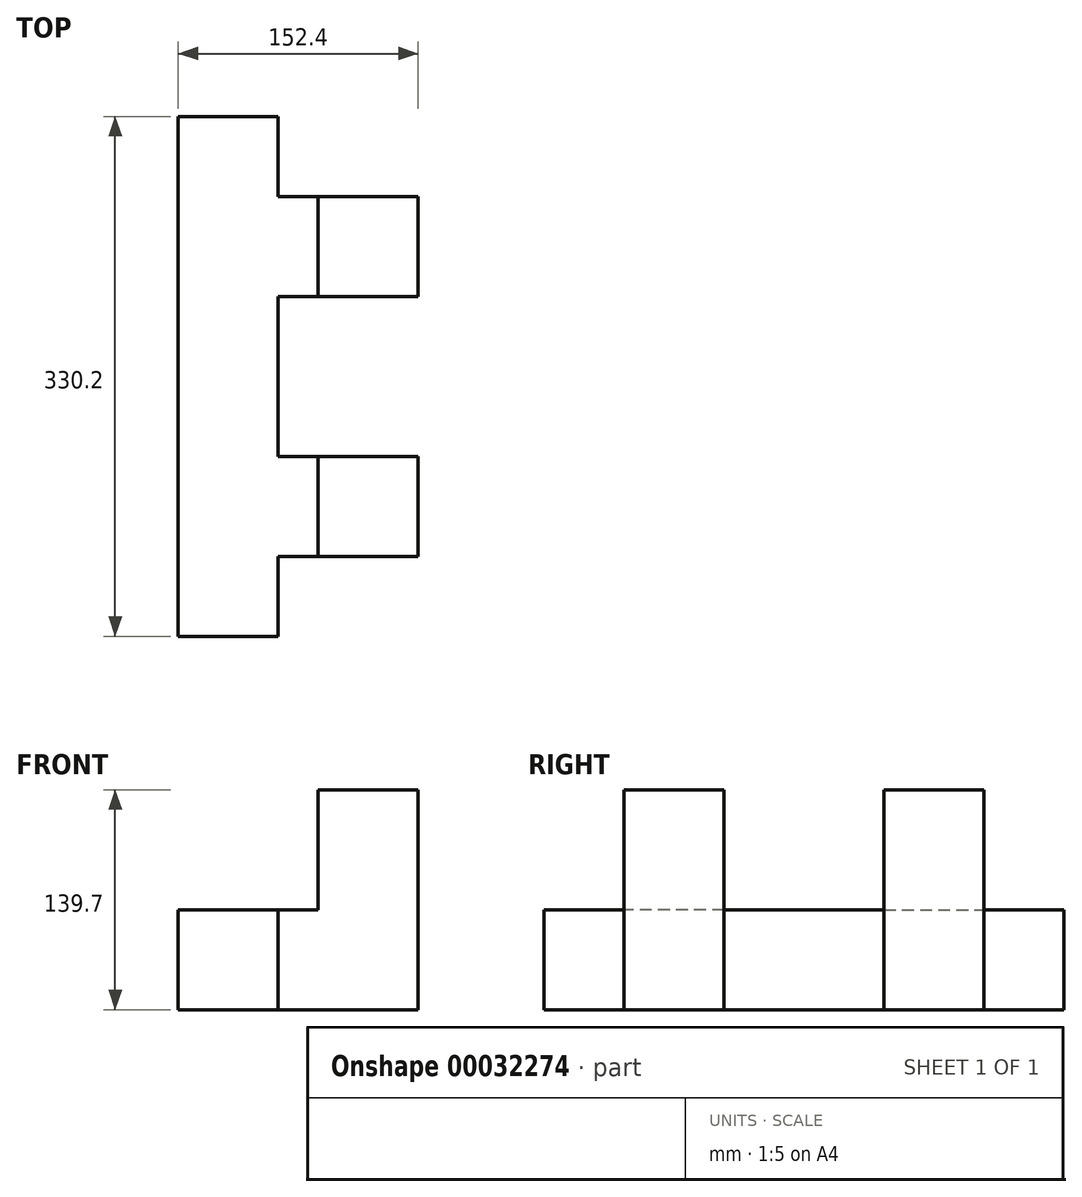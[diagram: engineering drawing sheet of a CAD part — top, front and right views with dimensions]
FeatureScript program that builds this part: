
annotation { "Feature Type Name" : "Feature", "Feature Type Description" : "" }
export const myFeature = defineFeature(function(context is Context, id is Id, definition is map)
    precondition{}
    {
        {
            var Q0;
            Q0=qCreatedBy(makeId("Top.planeOp"),FACE);
            var sketch = newSketch(context, id + "F0", { "sketchPlane" : qUnion([Q0])});
            skLineSegment(sketch, "E0", {"start": v(0, 0) * mm, "end": v(0, -330.2) * mm});
            skLineSegment(sketch, "E1", {"start": v(0, -330.2) * mm, "end": v(63.5, -330.2) * mm});
            skLineSegment(sketch, "E2", {"start": v(63.5, -330.2) * mm, "end": v(63.5, -279.4) * mm});
            skLineSegment(sketch, "E3", {"start": v(63.5, -279.4) * mm, "end": v(152.4, -279.4) * mm});
            skLineSegment(sketch, "E4", {"start": v(152.4, -279.4) * mm, "end": v(152.4, -215.9) * mm});
            skLineSegment(sketch, "E5", {"start": v(152.4, -215.9) * mm, "end": v(63.5, -215.9) * mm});
            skLineSegment(sketch, "E6", {"start": v(63.5, -215.9) * mm, "end": v(63.5, -114.3) * mm});
            skLineSegment(sketch, "E7", {"start": v(63.5, -114.3) * mm, "end": v(152.4, -114.3) * mm});
            skLineSegment(sketch, "E8", {"start": v(152.4, -114.3) * mm, "end": v(152.4, -50.8) * mm});
            skLineSegment(sketch, "E9", {"start": v(152.4, -50.8) * mm, "end": v(63.5, -50.8) * mm});
            skLineSegment(sketch, "E10", {"start": v(63.5, -50.8) * mm, "end": v(63.5, 0) * mm});
            skLineSegment(sketch, "E11", {"start": v(63.5, 0) * mm, "end": v(0, 0) * mm});
            skSolve(sketch);
        }
        {
            var Q0;
            Q0=makeQuery(id+"F0.imprint","IMPRINT",FACE,{"disambiguationData":[TD([[makeQuery(id+"F0.imprint","IMPRINT",EDGE,{"derivedFrom":sQuery(id+"F0.wireOp",EDGE,"E0")}),1.0]])]});
            extrude(context, id + "F1", {"entities" : qUnion([Q0]), "depth" : 63.5 * mm});
        }
        {
            var Q0;
            Q0=makeQuery(id+"F1.opExtrude","CAP_FACE",FACE,{"disambiguationData":[OSD([sQuery(id+"F0.wireOp",EDGE,"E0"),sQuery(id+"F0.wireOp",EDGE,"E1"),sQuery(id+"F0.wireOp",EDGE,"E2"),sQuery(id+"F0.wireOp",EDGE,"E3"),sQuery(id+"F0.wireOp",EDGE,"E4"),sQuery(id+"F0.wireOp",EDGE,"E5"),sQuery(id+"F0.wireOp",EDGE,"E6"),sQuery(id+"F0.wireOp",EDGE,"E7"),sQuery(id+"F0.wireOp",EDGE,"E8"),sQuery(id+"F0.wireOp",EDGE,"E9"),sQuery(id+"F0.wireOp",EDGE,"E10"),sQuery(id+"F0.wireOp",EDGE,"E11")])],"isStart":false});
            var sketch = newSketch(context, id + "F2", { "sketchPlane" : qUnion([Q0])});
            skLineSegment(sketch, "E12.bottom", {"start": v(152.4, -215.9) * mm, "end": v(88.9, -215.9) * mm});
            skLineSegment(sketch, "E12.top", {"start": v(152.4, -279.4) * mm, "end": v(88.9, -279.4) * mm});
            skLineSegment(sketch, "E12.left", {"start": v(152.4, -215.9) * mm, "end": v(152.4, -279.4) * mm});
            skLineSegment(sketch, "E12.right", {"start": v(88.9, -215.9) * mm, "end": v(88.9, -279.4) * mm});
            skLineSegment(sketch, "E13.bottom", {"start": v(152.4, -114.3) * mm, "end": v(88.9, -114.3) * mm});
            skLineSegment(sketch, "E13.top", {"start": v(152.4, -50.8) * mm, "end": v(88.9, -50.8) * mm});
            skLineSegment(sketch, "E13.left", {"start": v(152.4, -114.3) * mm, "end": v(152.4, -50.8) * mm});
            skLineSegment(sketch, "E13.right", {"start": v(88.9, -114.3) * mm, "end": v(88.9, -50.8) * mm});
            skSolve(sketch);
        }
        {
            var Q0;
            Q0=makeQuery(id+"F2.imprint","IMPRINT",FACE,{"disambiguationData":[TD([[makeQuery(id+"F2.imprint","IMPRINT",EDGE,{"derivedFrom":sQuery(id+"F2.wireOp",EDGE,"E13.bottom")}),1.0]])]});
            var Q1;
            Q1=makeQuery(id+"F2.imprint","IMPRINT",FACE,{"disambiguationData":[TD([[makeQuery(id+"F2.imprint","IMPRINT",EDGE,{"derivedFrom":sQuery(id+"F2.wireOp",EDGE,"E12.bottom")}),1.0]])]});
            extrude(context, id + "F3", {"entities" : qUnion([Q0, Q1]), "operationType" : NewBodyOperationType.ADD, "depth" : 76.2 * mm});
        }
    });
